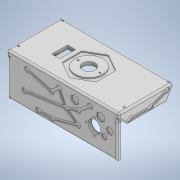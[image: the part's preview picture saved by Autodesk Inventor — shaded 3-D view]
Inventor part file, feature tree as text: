
AUTODESK INVENTOR PART (.ipt)
format: ipt  version: 2022 (Build 260153000, 153)  size: 631,296 bytes
history: native  units: in
note: dims shown in document units (in); Inventor stores cm internally (conversion verified against a paired STEP export)
features: extrude x18, sketch x17, projected_geometry x5, fillet x2, mirror x1
ambient origin geometry x8: Origin, YZ Plane, XZ Plane, XY Plane, X Axis, Y Axis, Z Axis, Center Point
bodies: Solid1 (feature_tree)
feature tree (43):
  extrude  "Extrusion1"  Depth=7.9in
  extrude  "Extrusion3"  Depth=0.25in
  extrude  "Extrusion4"  Depth=0.9055in
  extrude  "Extrusion5"  Depth=1.0in TaperAngle=0.0deg
  extrude  "Extrusion6"  Depth=0.35in
  sketch  "Sketch7"  dims[d20=0.35in d21=0.35in]
  extrude  "Extrusion7"  Depth=0.35in
  extrude  "Extrusion8"  Depth=0.35in
  sketch  "Sketch9"  dims[d24=1.0in d25=0.525in]
  extrude  "Extrusion9"  Depth=0.525in
  extrude  "Extrusion10"  Depth=2.825in
  extrude  "Extrusion11"  Depth=0.52in
  extrude  "Extrusion12"  Depth=3.7in
  extrude  "Extrusion13"  Depth=1.0in
  extrude  "Extrusion14"  Depth=0.0875in
  extrude  "Extrusion15"  Depth=0.0625in TaperAngle=0.0deg
  extrude  "Extrusion16"  Depth=0.511in
  extrude  "Extrusion17"  Depth=0.0625in TaperAngle=0.0deg
  extrude  "Extrusion18"  Depth=0.3937in
  mirror  "Mirror1"
  fillet  "Fillet4"  Radius=0.125in
  fillet  "Fillet5"  Radius=0.12in
  extrude  "Extrusion19"  Depth=0.3937in
  sketch  "Sketch1"  dims[d0=1.875in d1=7.9in]
  sketch  "Sketch3"  dims[d2=0.1181in d3=0.25in]
  sketch  "Sketch4"  dims[d4=0.25in d5=0.0in d13=0.9055in]
  projected_geometry  "Projected Loop2"
  sketch  "Sketch5"  dims[d14=1.65in d15=1.0in d16=0.0in]
  projected_geometry  "Projected Loop3"
  sketch  "Sketch6"  dims[d17=0.35in d19=0.35in]
  projected_geometry  "Projected Loop4"
  sketch  "Sketch8"  dims[d22=0.35in d23=0.35in]
  projected_geometry  "Projected Loop5"
  sketch  "Sketch10"  dims[d26=1.95in d27=2.825in]
  sketch  "Sketch11"  dims[d30=1.18in d31=0.52in]
  sketch  "Sketch12"  dims[d32=1.36in d33=3.7in]
  sketch  "Sketch13"  dims[d34=3.14in d35=1.0in]
  projected_geometry  "Projected Loop6"
  sketch  "Sketch14"  dims[d36=0.0875in d37=0.0875in]
  sketch  "Sketch15"  dims[d38=0.0875in d43=0.0625in d44=0.0in]
  sketch  "Sketch17"  dims[d45=0.611in d46=0.511in]
  sketch  "Sketch18"  dims[d47=0.411in d48=0.0625in d49=0.0in]
  sketch  "Sketch19"  dims[d51=3.55in d52=0.25in d53=0.125in d54=0.12in d55=0.12in d56=0.375in d57=0.12in d58=0.375in d59=0.12in d60=0.25in d61=0.0in d62=2.84in d63=2.0in d64=0.9055in d65=0.25in d66=0.0in d67=0.0625in d68=0.0in d72=1.1378in d73=0.5748in d74=1.834in d75=1.3311in d76=250.0in d77=0.0in d78=0.35in d80=0.0875in d81=0.0875in d82=0.0875in d83=0.0875in d84=0.0875in d85=0.0875in d86=3.707in d87=1.0in d88=0.0in d89=2.775in d90=1.0in d91=0.0in d92=0.5906in d93=0.1181in d96=1.0in d97=0.0in d98=0.5906in d99=0.1181in d100=0.5906in d101=0.1181in d102=0.7874in d103=0.1181in d104=0.7874in d105=0.1181in d106=1.0in d107=0.0in d108=0.2405in d109=165.0deg d110=0.9843in d111=0.35in d112=0.35in d113=0.35in d114=0.0875in d115=0.0875in d116=1.0in d117=0.0in d119=0.125in d120=0.1181in d121=0.125in d122=0.1181in d123=1.0in d124=0.0in d125=1.0in d126=0.0in d129=0.1181in d130=0.0in d131=0.3in d132=0.1in d133=1.5in d134=0.35in d135=0.35in d136=0.35in d137=0.0875in d138=0.0875in d139=0.0591in d140=0.0in d141=0.125in d142=0.125in d143=0.25in d144=0.25in d145=0.25in d146=0.25in d147=0.1181in d148=0.1181in d149=0.1181in d150=0.1181in d151=0.1181in d152=0.1181in d153=0.1181in d154=0.1181in d155=0.3937in d156=0.0in]
